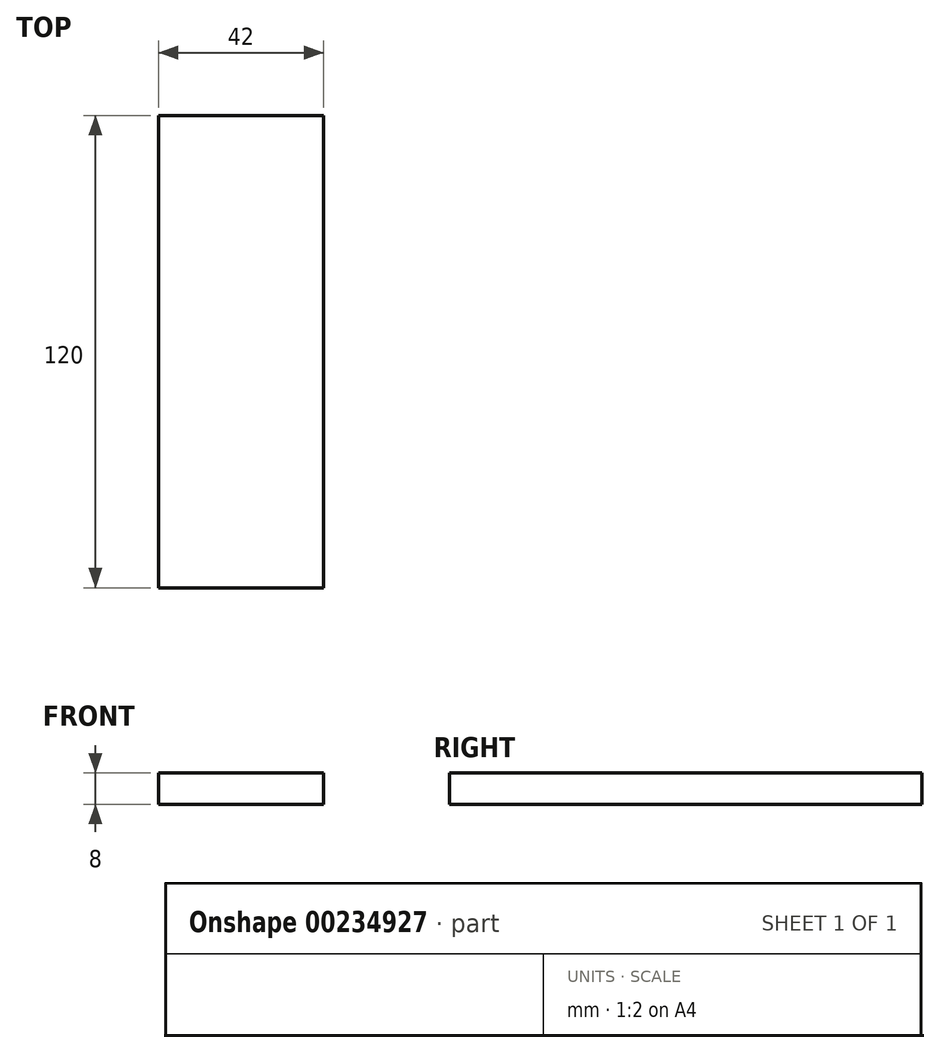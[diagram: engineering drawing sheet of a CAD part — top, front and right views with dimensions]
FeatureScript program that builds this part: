
annotation { "Feature Type Name" : "Feature", "Feature Type Description" : "" }
export const myFeature = defineFeature(function(context is Context, id is Id, definition is map)
    precondition{}
    {
        {
            var Q0;
            Q0=qCreatedBy(makeId("Top.planeOp"),FACE);
            var sketch = newSketch(context, id + "F0", { "sketchPlane" : qUnion([Q0])});
            skLineSegment(sketch, "E0.bottom", {"start": v(21, 60) * mm, "end": v(-21, 60) * mm});
            skLineSegment(sketch, "E0.top", {"start": v(21, -60) * mm, "end": v(-21, -60) * mm});
            skLineSegment(sketch, "E0.left", {"start": v(21, 60) * mm, "end": v(21, -60) * mm});
            skLineSegment(sketch, "E0.right", {"start": v(-21, 60) * mm, "end": v(-21, -60) * mm});
            skPoint(sketch, "E0.middle", {"position": v(0, 0) * mm});
            skSolve(sketch);
        }
        {
            var Q0;
            Q0 = qSketchRegion(id + "F0", true);
            extrude(context, id + "F1", {"entities" : qUnion([Q0]), "depth" : 8 * mm, "offsetDistance" : 25 * mm});
        }
    });
